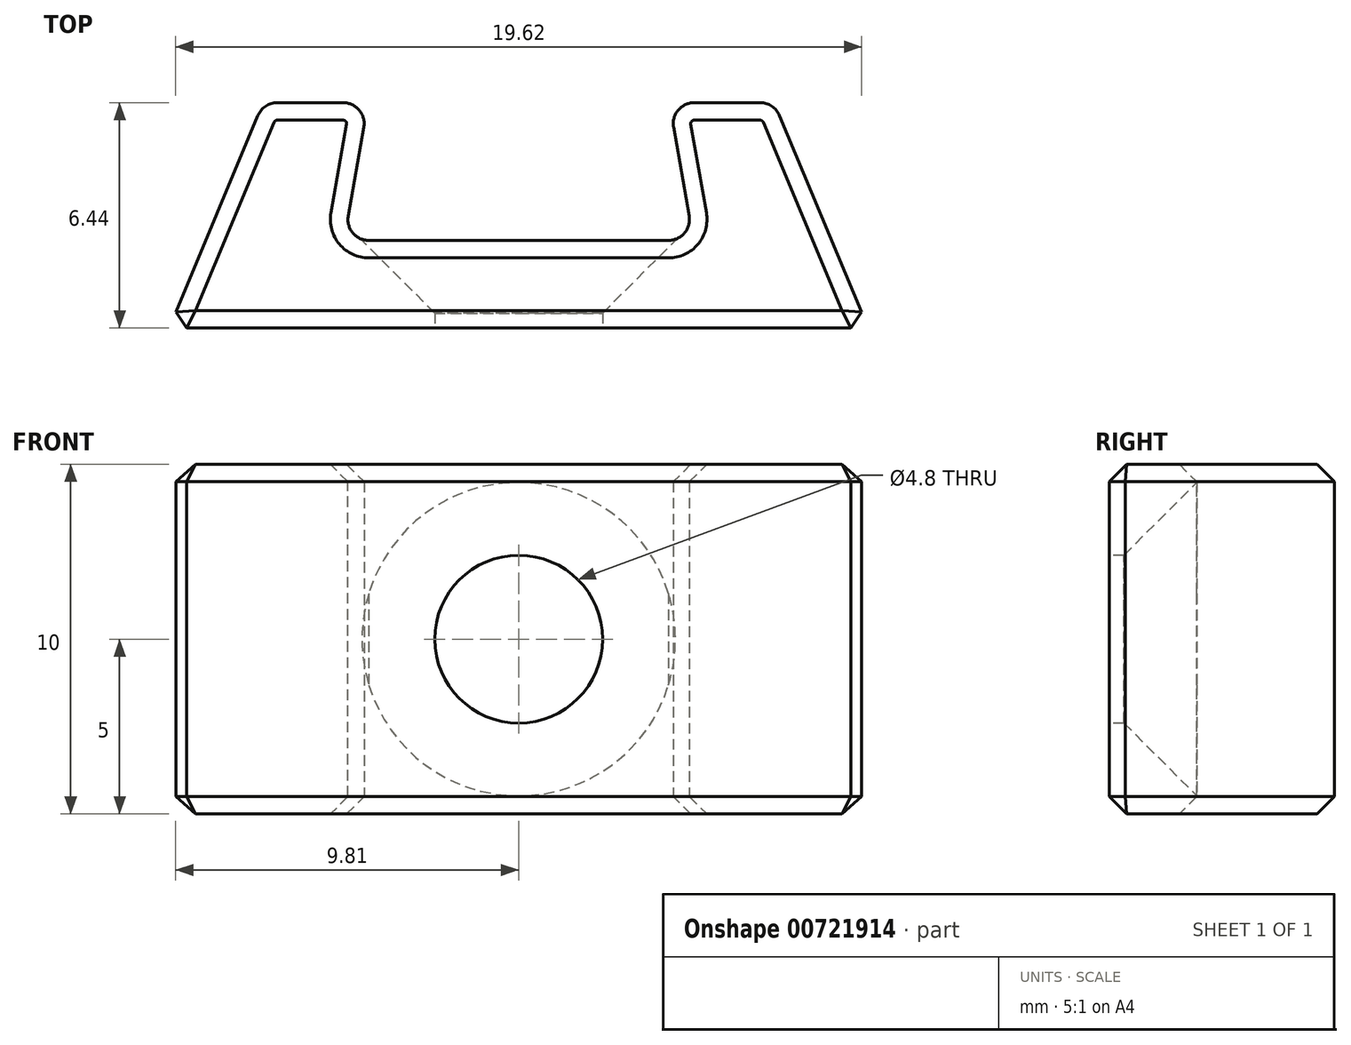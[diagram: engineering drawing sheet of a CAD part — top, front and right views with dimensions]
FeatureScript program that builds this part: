
annotation { "Feature Type Name" : "Feature", "Feature Type Description" : "" }
export const myFeature = defineFeature(function(context is Context, id is Id, definition is map)
    precondition{}
    {
        {
            var Q0;
            Q0=qCreatedBy(makeId("Top.planeOp"),FACE);
            var sketch = newSketch(context, id + "F0", { "sketchPlane" : qUnion([Q0])});
            skLineSegment(sketch, "E0", {"start": v(-10, 0) * mm, "end": v(10, 0) * mm});
            skLineSegment(sketch, "E1", {"start": v(10, 0) * mm, "end": v(7.3, 6.44) * mm});
            skLineSegment(sketch, "E2", {"start": v(5, 2.5) * mm, "end": v(0, 2.5) * mm});
            skLineSegment(sketch, "E3", {"start": v(0, 2.5) * mm, "end": v(0, 9.08) * mm, "construction": true});
            skLineSegment(sketch, "E4", {"start": v(5, 2.5) * mm, "end": v(4.3, 6.44) * mm});
            skLineSegment(sketch, "E5", {"start": v(4.3, 6.44) * mm, "end": v(7.3, 6.44) * mm});
            skLineSegment(sketch, "E6.MirrorCS", {"start": v(-5, 2.5) * mm, "end": v(0, 2.5) * mm});
            skLineSegment(sketch, "E7.MirrorCS", {"start": v(-5, 2.5) * mm, "end": v(-4.3, 6.44) * mm});
            skLineSegment(sketch, "E8.MirrorCS", {"start": v(-4.3, 6.44) * mm, "end": v(-7.3, 6.44) * mm});
            skLineSegment(sketch, "E9.MirrorCS", {"start": v(-10, 0) * mm, "end": v(-7.3, 6.44) * mm});
            skSolve(sketch);
        }
        {
            var Q0;
            Q0=makeQuery(id+"F0.imprint","IMPRINT",FACE,{"disambiguationData":[TD([[makeQuery(id+"F0.imprint","IMPRINT",EDGE,{"derivedFrom":sQuery(id+"F0.wireOp",EDGE,"E0")}),1.0]])]});
            extrude(context, id + "F1", {"entities" : qUnion([Q0]), "depth" : 10 * mm, "offsetDistance" : 25 * mm});
        }
        {
            var Q0;
            Q0=makeQuery(id+"F1.opExtrude","SWEPT_EDGE",EDGE,{"disambiguationData":[OSD([sQuery(id+"F0.wireOp",EDGE,"E6.MirrorCS"),sQuery(id+"F0.wireOp",EDGE,"E7.MirrorCS")])]});
            var Q1;
            Q1=makeQuery(id+"F1.opExtrude","SWEPT_EDGE",EDGE,{"disambiguationData":[OSD([sQuery(id+"F0.wireOp",EDGE,"E8.MirrorCS"),sQuery(id+"F0.wireOp",EDGE,"E9.MirrorCS")])]});
            var Q2;
            Q2=makeQuery(id+"F1.opExtrude","SWEPT_EDGE",EDGE,{"disambiguationData":[OSD([sQuery(id+"F0.wireOp",EDGE,"E1"),sQuery(id+"F0.wireOp",EDGE,"E5")])]});
            var Q3;
            Q3=makeQuery(id+"F1.opExtrude","SWEPT_EDGE",EDGE,{"disambiguationData":[OSD([sQuery(id+"F0.wireOp",EDGE,"E2"),sQuery(id+"F0.wireOp",EDGE,"E4")])]});
            var Q4;
            Q4=makeQuery(id+"F1.opExtrude","SWEPT_EDGE",EDGE,{"disambiguationData":[OSD([sQuery(id+"F0.wireOp",EDGE,"E4"),sQuery(id+"F0.wireOp",EDGE,"E5")])]});
            var Q5;
            Q5=makeQuery(id+"F1.opExtrude","SWEPT_EDGE",EDGE,{"disambiguationData":[OSD([sQuery(id+"F0.wireOp",EDGE,"E7.MirrorCS"),sQuery(id+"F0.wireOp",EDGE,"E8.MirrorCS")])]});
            fillet(context, id + "F2", {"entities" : qUnion([Q0, Q1, Q2, Q3, Q4, Q5]), "tangentPropagation" : true, "radius" : 0.6 * mm, "defaultsChanged" : false, "vertexSettings" : [], "allowEdgeOverflow" : false});
        }
        {
            var Q0;
            Q0=makeQuery(id+"F1.opExtrude","SWEPT_FACE",FACE,{"disambiguationData":[OSD([sQuery(id+"F0.wireOp",EDGE,"E2"),sQuery(id+"F0.wireOp",EDGE,"E6.MirrorCS")])]});
            var sketch = newSketch(context, id + "F3", { "sketchPlane" : qUnion([Q0])});
            skPoint(sketch, "E10", {"position": v(0, 5) * mm});
            skPoint(sketch, "E10.positionSnap0", {"position": v(4.28, 5) * mm});
            skPoint(sketch, "E10.positionSnap1", {"position": v(0, 10) * mm});
            skSolve(sketch);
        }
        {
            var Q0;
            Q0=sQuery(id+"F3.wireOp",VERTEX,"E10");
            var Q1;
            Q1=makeQuery(id+"F1.opExtrude","SWEPT_BODY",BODY,{"disambiguationData":[OSD([sQuery(id+"F0.wireOp",EDGE,"E0"),sQuery(id+"F0.wireOp",EDGE,"E1"),sQuery(id+"F0.wireOp",EDGE,"E2"),sQuery(id+"F0.wireOp",EDGE,"E4"),sQuery(id+"F0.wireOp",EDGE,"E5"),sQuery(id+"F0.wireOp",EDGE,"E6.MirrorCS"),sQuery(id+"F0.wireOp",EDGE,"E7.MirrorCS"),sQuery(id+"F0.wireOp",EDGE,"E8.MirrorCS"),sQuery(id+"F0.wireOp",EDGE,"E9.MirrorCS")])]});
            hole(context, id + "F4", {"style" : HoleStyle.C_SINK, "endStyle" : HoleEndStyle.BLIND, "holeDiameter" : 4.8 * mm, "cSinkDiameter" : 8.96 * mm, "cSinkAngle" : 90 * degree, "majorDiameter" : 5 * mm, "holeDepth" : 4 * mm, "isTappedThrough" : true, "tappedDepth" : 12 * mm, "tapClearance" : 3, "locations" : qUnion([Q0]), "scope" : qUnion([Q1]), "startStyle" : HoleStartStyle.PART});
        }
        {
            var Q0;
            Q0=makeQuery(id+"F1.opExtrude","CAP_FACE",FACE,{"disambiguationData":[OSD([sQuery(id+"F0.wireOp",EDGE,"E0"),sQuery(id+"F0.wireOp",EDGE,"E1"),sQuery(id+"F0.wireOp",EDGE,"E2"),sQuery(id+"F0.wireOp",EDGE,"E4"),sQuery(id+"F0.wireOp",EDGE,"E5"),sQuery(id+"F0.wireOp",EDGE,"E6.MirrorCS"),sQuery(id+"F0.wireOp",EDGE,"E7.MirrorCS"),sQuery(id+"F0.wireOp",EDGE,"E8.MirrorCS"),sQuery(id+"F0.wireOp",EDGE,"E9.MirrorCS")])],"isStart":true});
            var Q1;
            Q1=makeQuery(id+"F1.opExtrude","CAP_FACE",FACE,{"disambiguationData":[OSD([sQuery(id+"F0.wireOp",EDGE,"E0"),sQuery(id+"F0.wireOp",EDGE,"E1"),sQuery(id+"F0.wireOp",EDGE,"E2"),sQuery(id+"F0.wireOp",EDGE,"E4"),sQuery(id+"F0.wireOp",EDGE,"E5"),sQuery(id+"F0.wireOp",EDGE,"E6.MirrorCS"),sQuery(id+"F0.wireOp",EDGE,"E7.MirrorCS"),sQuery(id+"F0.wireOp",EDGE,"E8.MirrorCS"),sQuery(id+"F0.wireOp",EDGE,"E9.MirrorCS")])],"isStart":false});
            var Q2;
            Q2=makeQuery(id+"F1.opExtrude","SWEPT_EDGE",EDGE,{"disambiguationData":[OSD([sQuery(id+"F0.wireOp",EDGE,"E0"),sQuery(id+"F0.wireOp",EDGE,"E9.MirrorCS")])]});
            var Q3;
            Q3=makeQuery(id+"F1.opExtrude","SWEPT_EDGE",EDGE,{"disambiguationData":[OSD([sQuery(id+"F0.wireOp",EDGE,"E0"),sQuery(id+"F0.wireOp",EDGE,"E1")])]});
            chamfer(context, id + "F5", {"entities" : qUnion([Q0, Q1, Q2, Q3]), "width" : 0.5 * mm, "tangentPropagation" : true});
        }
    });
